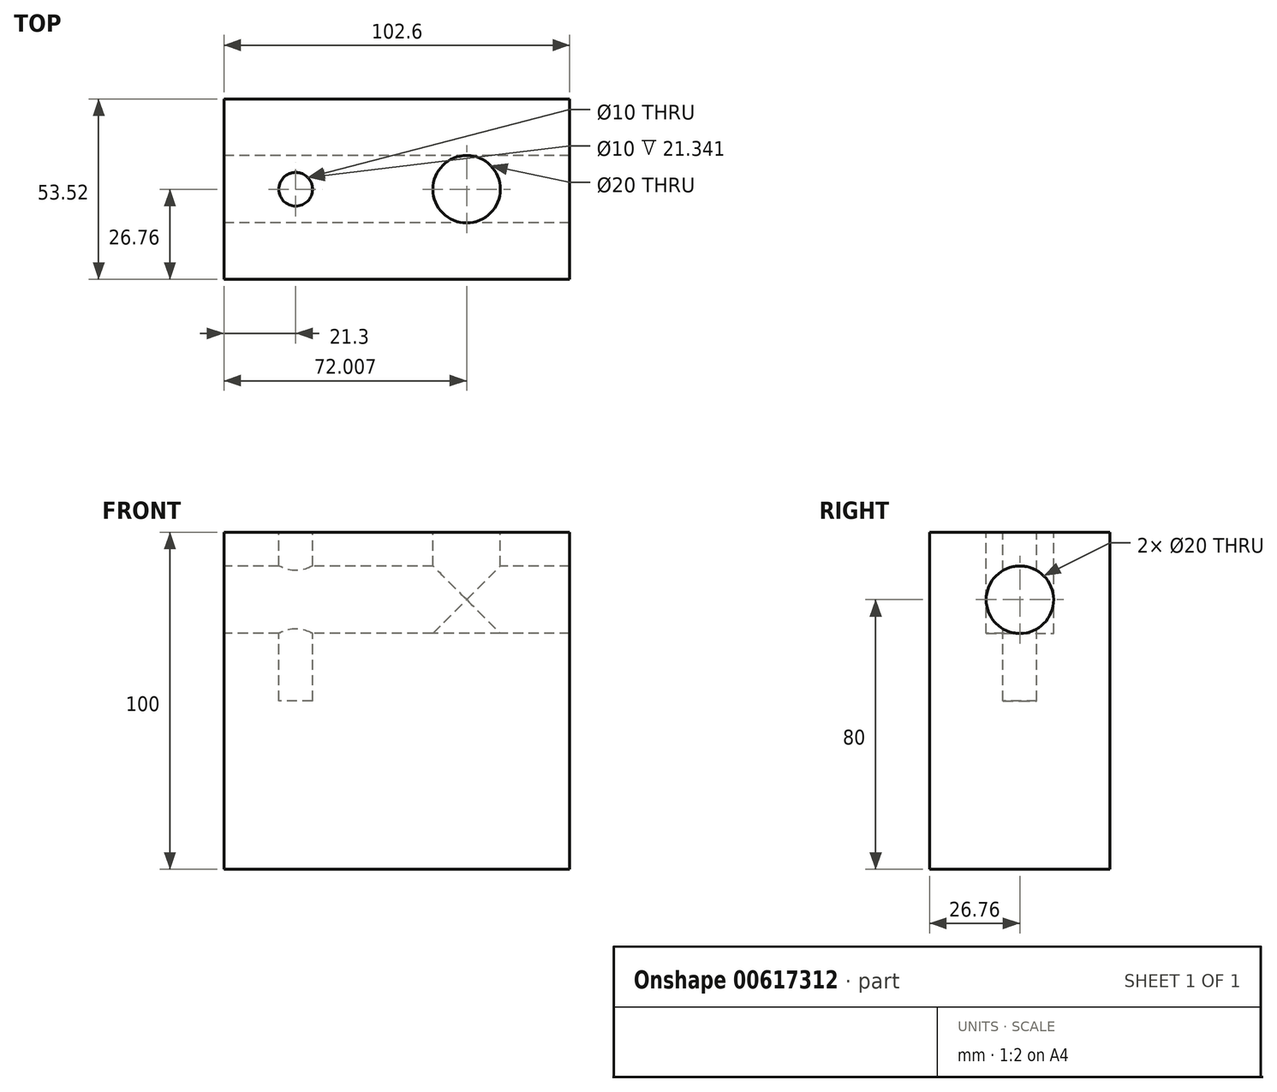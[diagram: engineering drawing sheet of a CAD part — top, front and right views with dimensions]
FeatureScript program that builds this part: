
annotation { "Feature Type Name" : "Feature", "Feature Type Description" : "" }
export const myFeature = defineFeature(function(context is Context, id is Id, definition is map)
    precondition{}
    {
        {
            var Q0;
            Q0=qCreatedBy(makeId("Top.planeOp"),FACE);
            var sketch = newSketch(context, id + "F0", { "sketchPlane" : qUnion([Q0])});
            skLineSegment(sketch, "E0.bottom", {"start": v(51.3, 26.76) * mm, "end": v(-51.3, 26.76) * mm});
            skLineSegment(sketch, "E0.top", {"start": v(51.3, -26.76) * mm, "end": v(-51.3, -26.76) * mm});
            skLineSegment(sketch, "E0.left", {"start": v(51.3, 26.76) * mm, "end": v(51.3, -26.76) * mm});
            skLineSegment(sketch, "E0.right", {"start": v(-51.3, 26.76) * mm, "end": v(-51.3, -26.76) * mm});
            skPoint(sketch, "E0.middle", {"position": v(0, 0) * mm});
            skSolve(sketch);
        }
        {
            var Q0;
            Q0=makeQuery(id+"F0.imprint","IMPRINT",FACE,{"disambiguationData":[TD([[makeQuery(id+"F0.imprint","IMPRINT",EDGE,{"derivedFrom":sQuery(id+"F0.wireOp",EDGE,"E0.bottom")}),1.0]])]});
            extrude(context, id + "F1", {"entities" : qUnion([Q0]), "depth" : 100 * mm, "offsetDistance" : 25 * mm});
        }
        {
            var Q0;
            Q0=makeQuery(id+"F1.opExtrude","CAP_FACE",FACE,{"disambiguationData":[OSD([sQuery(id+"F0.wireOp",EDGE,"E0.bottom"),sQuery(id+"F0.wireOp",EDGE,"E0.top"),sQuery(id+"F0.wireOp",EDGE,"E0.left"),sQuery(id+"F0.wireOp",EDGE,"E0.right")])],"isStart":false});
            var sketch = newSketch(context, id + "F2", { "sketchPlane" : qUnion([Q0])});
            skCircle(sketch, "E1", {"center": v(-30, 0) * mm, "radius": 5 * mm});
            skSolve(sketch);
        }
        {
            var Q0;
            Q0 = qSketchRegion(id + "F2", true);
            extrude(context, id + "F3", {"entities" : qUnion([Q0]), "operationType" : NewBodyOperationType.REMOVE, "oppositeDirection" : true, "depth" : 50 * mm, "offsetDistance" : 25 * mm});
        }
        {
            var Q0;
            Q0=makeQuery(id+"F1.opExtrude","SWEPT_FACE",FACE,{"disambiguationData":[OSD([sQuery(id+"F0.wireOp",EDGE,"E0.right")])]});
            var sketch = newSketch(context, id + "F4", { "sketchPlane" : qUnion([Q0])});
            skCircle(sketch, "E2", {"center": v(0, 80) * mm, "radius": 10 * mm});
            skPoint(sketch, "E2.centerSnap0", {"position": v(0, 0) * mm});
            skSolve(sketch);
        }
        {
            var Q0;
            Q0=makeQuery(id+"F4.imprint","IMPRINT",FACE,{"disambiguationData":[TD([[makeQuery(id+"F4.imprint","IMPRINT",EDGE,{"derivedFrom":sQuery(id+"F4.wireOp",EDGE,"E2")}),1.0]])]});
            extrude(context, id + "F5", {"entities" : qUnion([Q0]), "operationType" : NewBodyOperationType.REMOVE, "endBound" : BoundingType.THROUGH_ALL, "oppositeDirection" : true, "depth" : 25 * mm, "offsetDistance" : 25 * mm});
        }
        {
            var Q0;
            Q0=makeQuery(id+"F1.opExtrude","CAP_FACE",FACE,{"disambiguationData":[OSD([sQuery(id+"F0.wireOp",EDGE,"E0.bottom"),sQuery(id+"F0.wireOp",EDGE,"E0.top"),sQuery(id+"F0.wireOp",EDGE,"E0.left"),sQuery(id+"F0.wireOp",EDGE,"E0.right")])],"isStart":false});
            var sketch = newSketch(context, id + "F6", { "sketchPlane" : qUnion([Q0])});
            skCircle(sketch, "E3", {"center": v(20.7, 0) * mm, "radius": 10 * mm});
            skSolve(sketch);
        }
        {
            var Q0;
            Q0=makeQuery(id+"F6.imprint","IMPRINT",FACE,{"disambiguationData":[TD([[makeQuery(id+"F6.imprint","IMPRINT",EDGE,{"derivedFrom":sQuery(id+"F6.wireOp",EDGE,"E3")}),1.0]])]});
            extrude(context, id + "F7", {"entities" : qUnion([Q0]), "operationType" : NewBodyOperationType.REMOVE, "oppositeDirection" : true, "depth" : 30 * mm, "offsetDistance" : 25 * mm});
        }
    });
